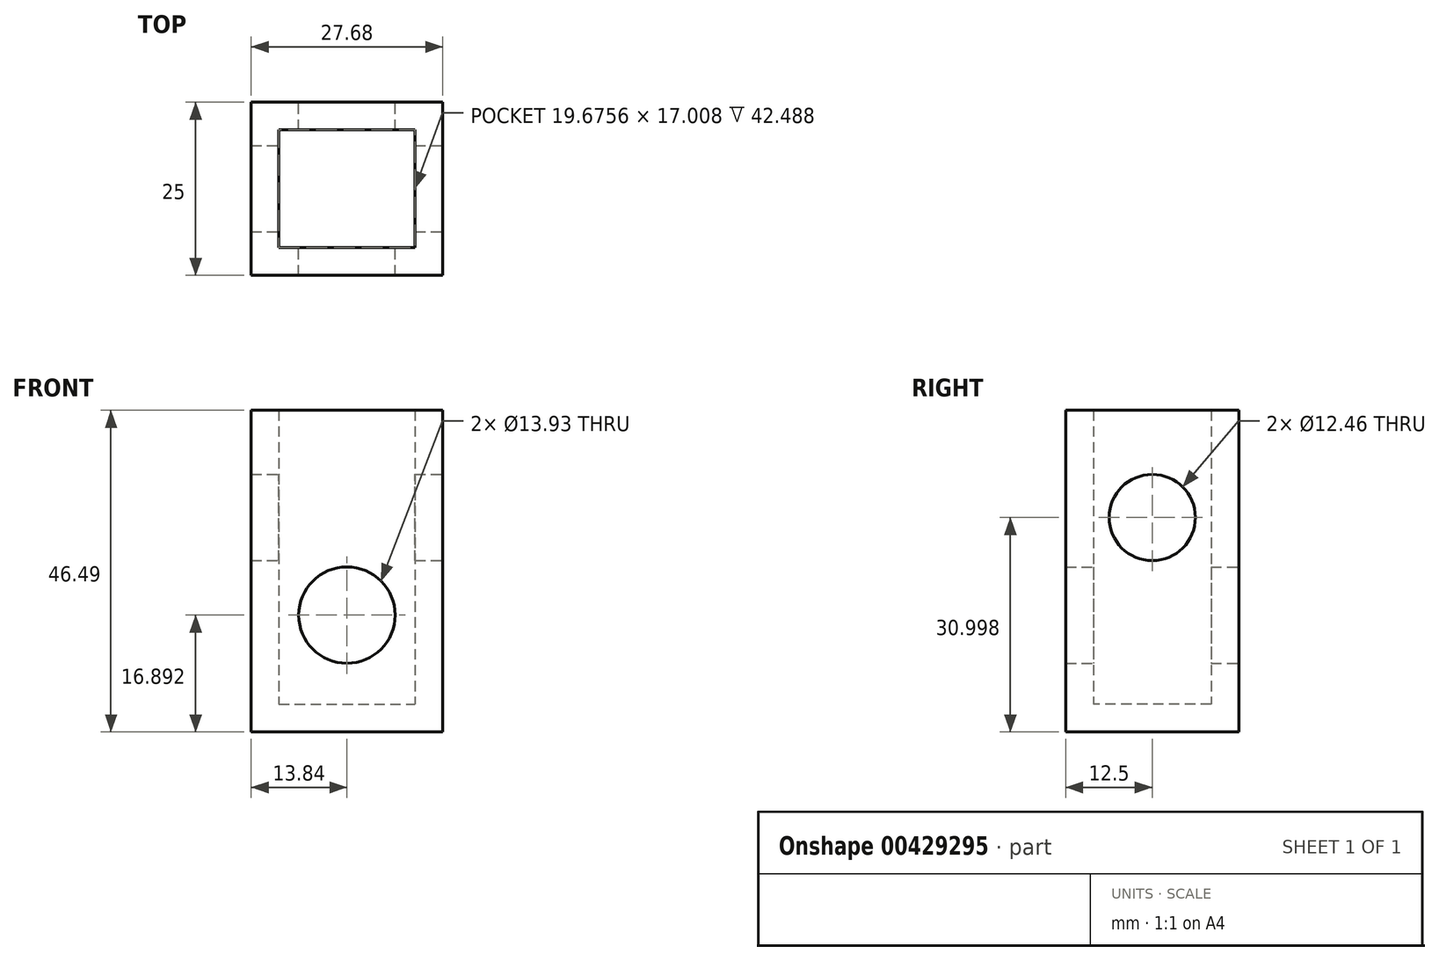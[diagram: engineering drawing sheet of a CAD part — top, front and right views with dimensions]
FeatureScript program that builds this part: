
annotation { "Feature Type Name" : "Feature", "Feature Type Description" : "" }
export const myFeature = defineFeature(function(context is Context, id is Id, definition is map)
    precondition{}
    {
        {
            var Q0;
            Q0=qCreatedBy(makeId("Top.planeOp"),FACE);
            var sketch = newSketch(context, id + "F0", { "sketchPlane" : qUnion([Q0])});
            skLineSegment(sketch, "E0.bottom", {"start": v(-13.84, 12.5) * mm, "end": v(13.84, 12.5) * mm});
            skLineSegment(sketch, "E0.top", {"start": v(-13.84, -12.5) * mm, "end": v(13.84, -12.5) * mm});
            skLineSegment(sketch, "E0.left", {"start": v(-13.84, 12.5) * mm, "end": v(-13.84, -12.5) * mm});
            skLineSegment(sketch, "E0.right", {"start": v(13.84, 12.5) * mm, "end": v(13.84, -12.5) * mm});
            skPoint(sketch, "E0.middle", {"position": v(0, 0) * mm});
            skSolve(sketch);
        }
        {
            var Q0;
            Q0 = qSketchRegion(id + "F0", true);
            extrude(context, id + "F1", {"entities" : qUnion([Q0]), "depth" : 46.5 * mm});
        }
        {
            var Q0;
            Q0=makeQuery(id+"F1.opExtrude","CAP_FACE",FACE,{"disambiguationData":[OSD([sQuery(id+"F0.wireOp",EDGE,"E0.bottom"),sQuery(id+"F0.wireOp",EDGE,"E0.top"),sQuery(id+"F0.wireOp",EDGE,"E0.left"),sQuery(id+"F0.wireOp",EDGE,"E0.right")])],"isStart":false});
            shell(context, id + "F2", {"entities" : qUnion([Q0]), "thickness" : 4 * mm});
        }
        {
            var Q0;
            Q0=qCreatedBy(makeId("Front.planeOp"),FACE);
            var sketch = newSketch(context, id + "F3", { "sketchPlane" : qUnion([Q0])});
            skCircle(sketch, "E1", {"center": v(0, 16.9) * mm, "radius": 6.97 * mm});
            skSolve(sketch);
        }
        {
            var Q0;
            Q0 = qSketchRegion(id + "F3", true);
            extrude(context, id + "F4", {"entities" : qUnion([Q0]), "operationType" : NewBodyOperationType.REMOVE, "endBound" : BoundingType.SYMMETRIC, "depth" : 78.53 * mm});
        }
        {
            var Q0;
            Q0=makeQuery(id+"F1.opExtrude","SWEPT_FACE",FACE,{"disambiguationData":[OSD([sQuery(id+"F0.wireOp",EDGE,"E0.right")])]});
            var sketch = newSketch(context, id + "F5", { "sketchPlane" : qUnion([Q0])});
            skCircle(sketch, "E2", {"center": v(0, 31) * mm, "radius": 6.23 * mm});
            skSolve(sketch);
        }
        {
            var Q0;
            Q0 = qSketchRegion(id + "F5", true);
            extrude(context, id + "F6", {"entities" : qUnion([Q0]), "operationType" : NewBodyOperationType.REMOVE, "endBound" : BoundingType.SYMMETRIC, "oppositeDirection" : true, "depth" : 60 * mm});
        }
    });
